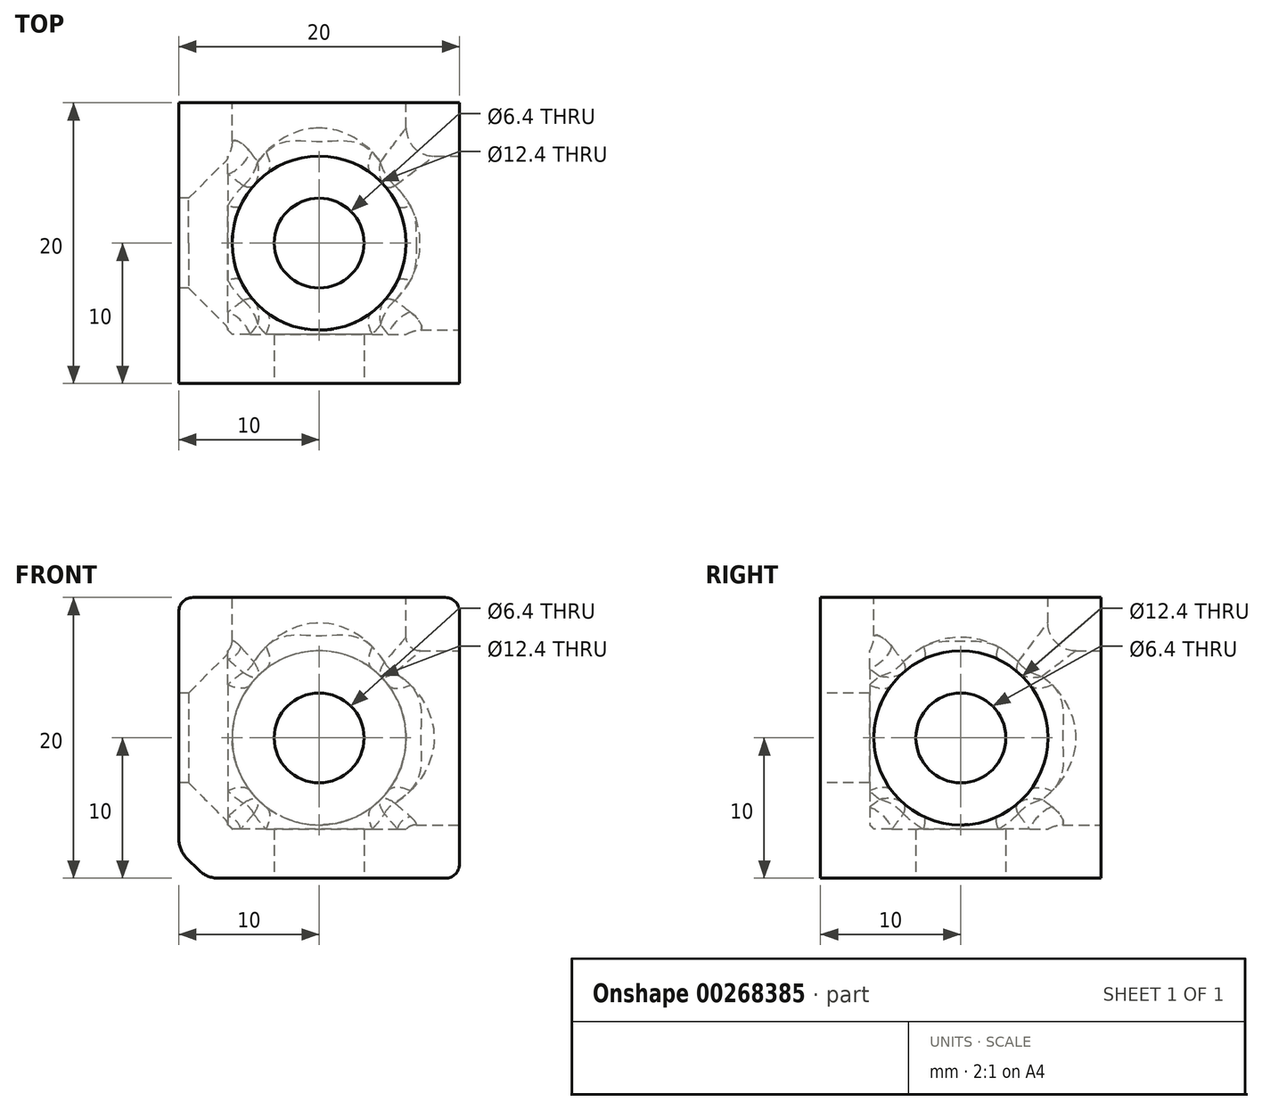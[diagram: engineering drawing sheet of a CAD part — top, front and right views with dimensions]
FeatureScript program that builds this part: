
annotation { "Feature Type Name" : "Feature", "Feature Type Description" : "" }
export const myFeature = defineFeature(function(context is Context, id is Id, definition is map)
    precondition{}
    {
        {
            var Q0;
            Q0=qCreatedBy(makeId("Top.planeOp"),FACE);
            var sketch = newSketch(context, id + "F0", { "sketchPlane" : qUnion([Q0])});
            skLineSegment(sketch, "E0.bottom", {"start": v(10, -10) * mm, "end": v(-10, -10) * mm});
            skLineSegment(sketch, "E0.top", {"start": v(10, 10) * mm, "end": v(-10, 10) * mm});
            skLineSegment(sketch, "E0.left", {"start": v(10, -10) * mm, "end": v(10, 10) * mm});
            skLineSegment(sketch, "E0.right", {"start": v(-10, -10) * mm, "end": v(-10, 10) * mm});
            skPoint(sketch, "E0.middle", {"position": v(0, 0) * mm});
            skSolve(sketch);
        }
        {
            var Q0;
            Q0=qSketchRegion(id+"F0",true);
            extrude(context, id + "F1", {"entities" : qUnion([Q0]), "depth" : 20 * mm});
        }
        {
            var Q0;
            Q0=makeQuery(id+"F1.opExtrude","SWEPT_FACE",FACE,{"disambiguationData":[OSD([sQuery(id+"F0.wireOp",EDGE,"E0.bottom")])]});
            var sketch = newSketch(context, id + "F2", { "sketchPlane" : qUnion([Q0])});
            skCircle(sketch, "E1", {"center": v(0, 10) * mm, "radius": 3.2 * mm});
            skPoint(sketch, "E1.centerSnap0", {"position": v(-10, 10) * mm});
            skSolve(sketch);
        }
        {
            var Q0;
            Q0=makeQuery(id+"F1.opExtrude","SWEPT_FACE",FACE,{"disambiguationData":[OSD([sQuery(id+"F0.wireOp",EDGE,"E0.right")])]});
            var sketch = newSketch(context, id + "F3", { "sketchPlane" : qUnion([Q0])});
            skCircle(sketch, "E2", {"center": v(0, 10) * mm, "radius": 3.2 * mm});
            skPoint(sketch, "E2.centerSnap0", {"position": v(0, 20) * mm});
            skPoint(sketch, "E2.centerSnap1", {"position": v(10, 10) * mm});
            skSolve(sketch);
        }
        {
            var Q0;
            Q0=makeQuery(id+"F1.opExtrude","CAP_FACE",FACE,{"disambiguationData":[OSD([sQuery(id+"F0.wireOp",EDGE,"E0.bottom"),sQuery(id+"F0.wireOp",EDGE,"E0.top"),sQuery(id+"F0.wireOp",EDGE,"E0.left"),sQuery(id+"F0.wireOp",EDGE,"E0.right")])],"isStart":true});
            var sketch = newSketch(context, id + "F4", { "sketchPlane" : qUnion([Q0])});
            skCircle(sketch, "E3", {"center": v(0, 0) * mm, "radius": 3.2 * mm});
            skSolve(sketch);
        }
        {
            var Q0;
            Q0=qSketchRegion(id+"F4",true);
            extrude(context, id + "F5", {"entities" : qUnion([Q0]), "operationType" : NewBodyOperationType.REMOVE, "endBound" : BoundingType.THROUGH_ALL, "oppositeDirection" : true, "depth" : 25 * mm});
        }
        {
            var Q0;
            Q0=makeQuery(id+"F2.imprint","IMPRINT",FACE,{"disambiguationData":[TD([[makeQuery(id+"F2.imprint","IMPRINT",EDGE,{"derivedFrom":sQuery(id+"F2.wireOp",EDGE,"E1")}),1.0]])]});
            extrude(context, id + "F6", {"entities" : qUnion([Q0]), "operationType" : NewBodyOperationType.REMOVE, "endBound" : BoundingType.THROUGH_ALL, "oppositeDirection" : true, "depth" : 25 * mm});
        }
        {
            var Q0;
            Q0=makeQuery(id+"F3.imprint","IMPRINT",FACE,{"disambiguationData":[TD([[makeQuery(id+"F3.imprint","IMPRINT",EDGE,{"derivedFrom":sQuery(id+"F3.wireOp",EDGE,"E2")}),1.0]])]});
            extrude(context, id + "F7", {"entities" : qUnion([Q0]), "operationType" : NewBodyOperationType.REMOVE, "endBound" : BoundingType.THROUGH_ALL, "oppositeDirection" : true, "depth" : 25 * mm});
        }
        {
            var Q0;
            Q0=makeQuery(id+"F1.opExtrude","CAP_FACE",FACE,{"disambiguationData":[OSD([sQuery(id+"F0.wireOp",EDGE,"E0.bottom"),sQuery(id+"F0.wireOp",EDGE,"E0.top"),sQuery(id+"F0.wireOp",EDGE,"E0.left"),sQuery(id+"F0.wireOp",EDGE,"E0.right")])],"isStart":false});
            var sketch = newSketch(context, id + "F8", { "sketchPlane" : qUnion([Q0])});
            skCircle(sketch, "E4", {"center": v(0, 0) * mm, "radius": 6.2 * mm});
            skSolve(sketch);
        }
        {
            var Q0;
            Q0=makeQuery(id+"F1.opExtrude","SWEPT_FACE",FACE,{"disambiguationData":[OSD([sQuery(id+"F0.wireOp",EDGE,"E0.top")])]});
            var sketch = newSketch(context, id + "F9", { "sketchPlane" : qUnion([Q0])});
            skCircle(sketch, "E5", {"center": v(0, 10) * mm, "radius": 6.2 * mm});
            skSolve(sketch);
        }
        {
            var Q0;
            Q0=makeQuery(id+"F1.opExtrude","SWEPT_FACE",FACE,{"disambiguationData":[OSD([sQuery(id+"F0.wireOp",EDGE,"E0.left")])]});
            var sketch = newSketch(context, id + "F10", { "sketchPlane" : qUnion([Q0])});
            skCircle(sketch, "E6", {"center": v(0, 10) * mm, "radius": 6.2 * mm});
            skSolve(sketch);
        }
        {
            var Q0;
            Q0=qSketchRegion(id+"F10",true);
            extrude(context, id + "F11", {"entities" : qUnion([Q0]), "operationType" : NewBodyOperationType.REMOVE, "oppositeDirection" : true, "depth" : 16.5 * mm});
        }
        {
            var Q0;
            Q0=makeQuery(id+"F9.imprint","IMPRINT",FACE,{"disambiguationData":[TD([[makeQuery(id+"F9.imprint","IMPRINT",EDGE,{"derivedFrom":sQuery(id+"F9.wireOp",EDGE,"E5")}),1.0]])]});
            extrude(context, id + "F12", {"entities" : qUnion([Q0]), "operationType" : NewBodyOperationType.REMOVE, "oppositeDirection" : true, "depth" : 16.5 * mm});
        }
        {
            var Q0;
            Q0=makeQuery(id+"F8.imprint","IMPRINT",FACE,{"disambiguationData":[TD([[makeQuery(id+"F8.imprint","IMPRINT",EDGE,{"derivedFrom":sQuery(id+"F8.wireOp",EDGE,"E4")}),1.0]])]});
            extrude(context, id + "F13", {"entities" : qUnion([Q0]), "operationType" : NewBodyOperationType.REMOVE, "oppositeDirection" : true, "depth" : 16.5 * mm});
        }
        {
            var Q0;
            Q0=makeQuery(id+"F11.boolean.opBoolean","INTERSECT",EDGE,{"derivedFrom":[makeQuery(id+"F7.boolean.opBoolean","COPY",FACE,{"disambiguationData":[TD([makeQuery(id+"F1.opExtrude","SWEPT_FACE",FACE,{"disambiguationData":[OSD([sQuery(id+"F0.wireOp",EDGE,"E0.right")])]})])],"derivedFrom":makeQuery(id+"F7.opExtrude","SWEPT_FACE",FACE,{"disambiguationData":[OSD([sQuery(id+"F3.wireOp",EDGE,"E2")])]})}),makeQuery(id+"F11.opExtrude","CAP_FACE",FACE,{"disambiguationData":[OSD([sQuery(id+"F10.wireOp",EDGE,"E6")])],"isStart":false})]});
            var Q1;
            Q1=makeQuery(id+"F13.boolean.opBoolean","COPY",EDGE,{"derivedFrom":makeQuery(id+"F13.opExtrude","CAP_EDGE",EDGE,{"disambiguationData":[OSD([sQuery(id+"F0.wireOp",EDGE,"E0.bottom"),sQuery(id+"F0.wireOp",EDGE,"E0.top"),sQuery(id+"F0.wireOp",EDGE,"E0.left"),sQuery(id+"F0.wireOp",EDGE,"E0.right"),sQuery(id+"F4.wireOp",EDGE,"E3")])],"isStart":false})});
            var Q2;
            Q2=makeQuery(id+"F12.boolean.opBoolean","COPY",EDGE,{"derivedFrom":makeQuery(id+"F12.opExtrude","CAP_EDGE",EDGE,{"disambiguationData":[OSD([sQuery(id+"F0.wireOp",EDGE,"E0.top"),sQuery(id+"F2.wireOp",EDGE,"E1")])],"isStart":false})});
            chamfer(context, id + "F14", {"entities" : qUnion([Q0, Q1, Q2]), "width" : 2.8 * mm, "tangentPropagation" : true});
        }
        {
            var Q0;
            Q0=makeQuery(id+"F1.opExtrude","CAP_EDGE",EDGE,{"disambiguationData":[OSD([sQuery(id+"F0.wireOp",EDGE,"E0.right")])],"isStart":true});
            chamfer(context, id + "F15", {"entities" : qUnion([Q0]), "width" : 2 * mm, "tangentPropagation" : true});
        }
        {
            var Q0;
            {var subQ0=sQuery(id+"F0.wireOp",EDGE,"E0.right");Q0=makeQuery(id+"F15.opChamfer","BLEND_EDGE",EDGE,{"blendedFrom":[makeQuery(id+"F1.opExtrude","CAP_EDGE",EDGE,{"disambiguationData":[OSD([subQ0])],"isStart":true}),makeQuery(id+"F1.opExtrude","CAP_FACE",FACE,{"disambiguationData":[OSD([sQuery(id+"F0.wireOp",EDGE,"E0.bottom"),sQuery(id+"F0.wireOp",EDGE,"E0.top"),sQuery(id+"F0.wireOp",EDGE,"E0.left"),subQ0])],"isStart":true})],"blendedInto":[makeQuery(id+"F1.opExtrude","CAP_FACE",FACE,{"disambiguationData":[OSD([sQuery(id+"F0.wireOp",EDGE,"E0.bottom"),sQuery(id+"F0.wireOp",EDGE,"E0.top"),sQuery(id+"F0.wireOp",EDGE,"E0.left"),subQ0])],"isStart":true})]});}
            var Q1;
            {var subQ0=sQuery(id+"F0.wireOp",EDGE,"E0.right");Q1=makeQuery(id+"F15.opChamfer","BLEND_EDGE",EDGE,{"blendedFrom":[makeQuery(id+"F1.opExtrude","CAP_EDGE",EDGE,{"disambiguationData":[OSD([subQ0])],"isStart":true}),makeQuery(id+"F1.opExtrude","SWEPT_FACE",FACE,{"disambiguationData":[OSD([subQ0])]})],"blendedInto":[makeQuery(id+"F1.opExtrude","SWEPT_FACE",FACE,{"disambiguationData":[OSD([subQ0])]})]});}
            fillet(context, id + "F16", {"entities" : qUnion([Q0, Q1]), "radius" : 2 * mm, "tangentPropagation" : true, "allowEdgeOverflow" : false});
        }
        {
            var Q0;
            {var subQ0=sQuery(id+"F9.wireOp",EDGE,"E5");Q0=makeQuery(id+"F13.boolean.opBoolean","INTERSECT",EDGE,{"disambiguationData":[OD(1.0)],"derivedFrom":[makeQuery(id+"F12.boolean.opBoolean","COPY",FACE,{"disambiguationData":[TD([makeQuery(id+"F12.opExtrude","CAP_FACE",FACE,{"disambiguationData":[OSD([sQuery(id+"F0.wireOp",EDGE,"E0.top"),sQuery(id+"F2.wireOp",EDGE,"E1"),subQ0])],"isStart":false})])],"derivedFrom":makeQuery(id+"F12.opExtrude","SWEPT_FACE",FACE,{"disambiguationData":[OSD([subQ0])]})}),makeQuery(id+"F13.opExtrude","SWEPT_FACE",FACE,{"disambiguationData":[OSD([sQuery(id+"F8.wireOp",EDGE,"E4")])]})]});}
            var Q1;
            Q1=makeQuery(id+"F12.boolean.opBoolean","INTERSECT",EDGE,{"disambiguationData":[OD(3.0)],"derivedFrom":[makeQuery(id+"F11.boolean.opBoolean","COPY",FACE,{"derivedFrom":makeQuery(id+"F11.opExtrude","SWEPT_FACE",FACE,{"disambiguationData":[OSD([sQuery(id+"F10.wireOp",EDGE,"E6")])]})}),makeQuery(id+"F12.opExtrude","SWEPT_FACE",FACE,{"disambiguationData":[OSD([sQuery(id+"F9.wireOp",EDGE,"E5")])]})]});
            var Q2;
            Q2=makeQuery(id+"F12.boolean.opBoolean","INTERSECT",EDGE,{"disambiguationData":[OD(1.0)],"derivedFrom":[makeQuery(id+"F11.boolean.opBoolean","COPY",FACE,{"derivedFrom":makeQuery(id+"F11.opExtrude","SWEPT_FACE",FACE,{"disambiguationData":[OSD([sQuery(id+"F10.wireOp",EDGE,"E6")])]})}),makeQuery(id+"F12.opExtrude","SWEPT_FACE",FACE,{"disambiguationData":[OSD([sQuery(id+"F9.wireOp",EDGE,"E5")])]})]});
            var Q3;
            {var subQ0=sQuery(id+"F9.wireOp",EDGE,"E5");Q3=makeQuery(id+"F13.boolean.opBoolean","INTERSECT",EDGE,{"disambiguationData":[OD(0.0)],"derivedFrom":[makeQuery(id+"F12.boolean.opBoolean","COPY",FACE,{"disambiguationData":[TD([makeQuery(id+"F12.opExtrude","CAP_FACE",FACE,{"disambiguationData":[OSD([sQuery(id+"F0.wireOp",EDGE,"E0.top"),sQuery(id+"F2.wireOp",EDGE,"E1"),subQ0])],"isStart":false})])],"derivedFrom":makeQuery(id+"F12.opExtrude","SWEPT_FACE",FACE,{"disambiguationData":[OSD([subQ0])]})}),makeQuery(id+"F13.opExtrude","SWEPT_FACE",FACE,{"disambiguationData":[OSD([sQuery(id+"F8.wireOp",EDGE,"E4")])]})]});}
            fillet(context, id + "F17", {"entities" : qUnion([Q0, Q1, Q2, Q3]), "radius" : 2 * mm, "tangentPropagation" : true, "allowEdgeOverflow" : false});
        }
        {
            var Q0;
            Q0=makeQuery(id+"F13.boolean.opBoolean","INTERSECT",EDGE,{"disambiguationData":[OD(1.0)],"derivedFrom":[makeQuery(id+"F12.boolean.opBoolean","COPY",FACE,{"disambiguationData":[TD([makeQuery(id+"F1.opExtrude","SWEPT_FACE",FACE,{"disambiguationData":[OSD([sQuery(id+"F0.wireOp",EDGE,"E0.top")])]})])],"derivedFrom":makeQuery(id+"F12.opExtrude","SWEPT_FACE",FACE,{"disambiguationData":[OSD([sQuery(id+"F9.wireOp",EDGE,"E5")])]})}),makeQuery(id+"F13.opExtrude","SWEPT_FACE",FACE,{"disambiguationData":[OSD([sQuery(id+"F8.wireOp",EDGE,"E4")])]})]});
            var Q1;
            Q1=makeQuery(id+"F12.boolean.opBoolean","INTERSECT",EDGE,{"disambiguationData":[OD(2.0)],"derivedFrom":[makeQuery(id+"F11.boolean.opBoolean","COPY",FACE,{"derivedFrom":makeQuery(id+"F11.opExtrude","SWEPT_FACE",FACE,{"disambiguationData":[OSD([sQuery(id+"F10.wireOp",EDGE,"E6")])]})}),makeQuery(id+"F12.opExtrude","SWEPT_FACE",FACE,{"disambiguationData":[OSD([sQuery(id+"F9.wireOp",EDGE,"E5")])]})]});
            var Q2;
            Q2=makeQuery(id+"F12.boolean.opBoolean","INTERSECT",EDGE,{"disambiguationData":[OD(0.0)],"derivedFrom":[makeQuery(id+"F11.boolean.opBoolean","COPY",FACE,{"derivedFrom":makeQuery(id+"F11.opExtrude","SWEPT_FACE",FACE,{"disambiguationData":[OSD([sQuery(id+"F10.wireOp",EDGE,"E6")])]})}),makeQuery(id+"F12.opExtrude","SWEPT_FACE",FACE,{"disambiguationData":[OSD([sQuery(id+"F9.wireOp",EDGE,"E5")])]})]});
            var Q3;
            Q3=makeQuery(id+"F13.boolean.opBoolean","INTERSECT",EDGE,{"disambiguationData":[OD(0.0)],"derivedFrom":[makeQuery(id+"F12.boolean.opBoolean","COPY",FACE,{"disambiguationData":[TD([makeQuery(id+"F1.opExtrude","SWEPT_FACE",FACE,{"disambiguationData":[OSD([sQuery(id+"F0.wireOp",EDGE,"E0.top")])]})])],"derivedFrom":makeQuery(id+"F12.opExtrude","SWEPT_FACE",FACE,{"disambiguationData":[OSD([sQuery(id+"F9.wireOp",EDGE,"E5")])]})}),makeQuery(id+"F13.opExtrude","SWEPT_FACE",FACE,{"disambiguationData":[OSD([sQuery(id+"F8.wireOp",EDGE,"E4")])]})]});
            fillet(context, id + "F18", {"entities" : qUnion([Q0, Q1, Q2, Q3]), "radius" : 2 * mm, "tangentPropagation" : true, "allowEdgeOverflow" : false});
        }
        {
            var Q0;
            {var subQ0=sQuery(id+"F10.wireOp",EDGE,"E6");Q0=makeQuery(id+"F13.boolean.opBoolean","INTERSECT",EDGE,{"disambiguationData":[OD(0.0)],"derivedFrom":[makeQuery(id+"F12.boolean.opBoolean","SPLIT",FACE,{"disambiguationData":[TD([makeQuery(id+"F11.boolean.opBoolean","COPY",FACE,{"derivedFrom":makeQuery(id+"F11.opExtrude","CAP_FACE",FACE,{"disambiguationData":[OSD([subQ0])],"isStart":false})})])],"derivedFrom":makeQuery(id+"F11.boolean.opBoolean","COPY",FACE,{"derivedFrom":makeQuery(id+"F11.opExtrude","SWEPT_FACE",FACE,{"disambiguationData":[OSD([subQ0])]})})}),makeQuery(id+"F13.opExtrude","SWEPT_FACE",FACE,{"disambiguationData":[OSD([sQuery(id+"F8.wireOp",EDGE,"E4")])]})]});}
            var Q1;
            {var subQ0=sQuery(id+"F10.wireOp",EDGE,"E6");Q1=makeQuery(id+"F13.boolean.opBoolean","INTERSECT",EDGE,{"disambiguationData":[OD(1.0)],"derivedFrom":[makeQuery(id+"F12.boolean.opBoolean","SPLIT",FACE,{"disambiguationData":[TD([makeQuery(id+"F11.boolean.opBoolean","COPY",FACE,{"derivedFrom":makeQuery(id+"F11.opExtrude","CAP_FACE",FACE,{"disambiguationData":[OSD([subQ0])],"isStart":false})})])],"derivedFrom":makeQuery(id+"F11.boolean.opBoolean","COPY",FACE,{"derivedFrom":makeQuery(id+"F11.opExtrude","SWEPT_FACE",FACE,{"disambiguationData":[OSD([subQ0])]})})}),makeQuery(id+"F13.opExtrude","SWEPT_FACE",FACE,{"disambiguationData":[OSD([sQuery(id+"F8.wireOp",EDGE,"E4")])]})]});}
            var Q2;
            Q2=makeQuery(id+"F13.boolean.opBoolean","INTERSECT",EDGE,{"disambiguationData":[OD(0.0)],"derivedFrom":[makeQuery(id+"F12.boolean.opBoolean","SPLIT",FACE,{"disambiguationData":[TD([makeQuery(id+"F1.opExtrude","SWEPT_FACE",FACE,{"disambiguationData":[OSD([sQuery(id+"F0.wireOp",EDGE,"E0.left")])]})])],"derivedFrom":makeQuery(id+"F11.boolean.opBoolean","COPY",FACE,{"derivedFrom":makeQuery(id+"F11.opExtrude","SWEPT_FACE",FACE,{"disambiguationData":[OSD([sQuery(id+"F10.wireOp",EDGE,"E6")])]})})}),makeQuery(id+"F13.opExtrude","SWEPT_FACE",FACE,{"disambiguationData":[OSD([sQuery(id+"F8.wireOp",EDGE,"E4")])]})]});
            var Q3;
            Q3=makeQuery(id+"F13.boolean.opBoolean","INTERSECT",EDGE,{"disambiguationData":[OD(1.0)],"derivedFrom":[makeQuery(id+"F12.boolean.opBoolean","SPLIT",FACE,{"disambiguationData":[TD([makeQuery(id+"F1.opExtrude","SWEPT_FACE",FACE,{"disambiguationData":[OSD([sQuery(id+"F0.wireOp",EDGE,"E0.left")])]})])],"derivedFrom":makeQuery(id+"F11.boolean.opBoolean","COPY",FACE,{"derivedFrom":makeQuery(id+"F11.opExtrude","SWEPT_FACE",FACE,{"disambiguationData":[OSD([sQuery(id+"F10.wireOp",EDGE,"E6")])]})})}),makeQuery(id+"F13.opExtrude","SWEPT_FACE",FACE,{"disambiguationData":[OSD([sQuery(id+"F8.wireOp",EDGE,"E4")])]})]});
            fillet(context, id + "F19", {"entities" : qUnion([Q0, Q1, Q2, Q3]), "radius" : 1 * mm, "tangentPropagation" : true, "allowEdgeOverflow" : false});
        }
        {
            var Q0;
            {var subQ0=makeQuery(id+"F11.opExtrude","CAP_FACE",FACE,{"disambiguationData":[OSD([sQuery(id+"F10.wireOp",EDGE,"E6")])],"isStart":false});Q0=makeQuery(id+"F14.opChamfer","BLEND_EDGE",EDGE,{"blendedFrom":[makeQuery(id+"F11.boolean.opBoolean","INTERSECT",EDGE,{"derivedFrom":[makeQuery(id+"F7.boolean.opBoolean","COPY",FACE,{"disambiguationData":[TD([makeQuery(id+"F1.opExtrude","SWEPT_FACE",FACE,{"disambiguationData":[OSD([sQuery(id+"F0.wireOp",EDGE,"E0.right")])]})])],"derivedFrom":makeQuery(id+"F7.opExtrude","SWEPT_FACE",FACE,{"disambiguationData":[OSD([sQuery(id+"F3.wireOp",EDGE,"E2")])]})}),subQ0]}),makeQuery(id+"F11.boolean.opBoolean","COPY",FACE,{"derivedFrom":subQ0})],"blendedInto":[makeQuery(id+"F11.boolean.opBoolean","COPY",FACE,{"derivedFrom":subQ0})]});}
            var Q1;
            {var subQ0=sQuery(id+"F2.wireOp",EDGE,"E1");var subQ1=sQuery(id+"F0.wireOp",EDGE,"E0.top");Q1=makeQuery(id+"F14.opChamfer","BLEND_EDGE",EDGE,{"blendedFrom":[makeQuery(id+"F12.boolean.opBoolean","COPY",EDGE,{"derivedFrom":makeQuery(id+"F12.opExtrude","CAP_EDGE",EDGE,{"disambiguationData":[OSD([subQ1,subQ0])],"isStart":false})}),makeQuery(id+"F12.boolean.opBoolean","COPY",FACE,{"derivedFrom":makeQuery(id+"F12.opExtrude","CAP_FACE",FACE,{"disambiguationData":[OSD([subQ1,subQ0,sQuery(id+"F9.wireOp",EDGE,"E5")])],"isStart":false})})],"blendedInto":[makeQuery(id+"F12.boolean.opBoolean","COPY",FACE,{"derivedFrom":makeQuery(id+"F12.opExtrude","CAP_FACE",FACE,{"disambiguationData":[OSD([subQ1,subQ0,sQuery(id+"F9.wireOp",EDGE,"E5")])],"isStart":false})})]});}
            var Q2;
            {var subQ0=sQuery(id+"F4.wireOp",EDGE,"E3");var subQ1=sQuery(id+"F0.wireOp",EDGE,"E0.right");var subQ2=sQuery(id+"F0.wireOp",EDGE,"E0.left");var subQ3=sQuery(id+"F0.wireOp",EDGE,"E0.top");var subQ4=sQuery(id+"F0.wireOp",EDGE,"E0.bottom");Q2=makeQuery(id+"F14.opChamfer","BLEND_EDGE",EDGE,{"blendedFrom":[makeQuery(id+"F13.boolean.opBoolean","COPY",EDGE,{"derivedFrom":makeQuery(id+"F13.opExtrude","CAP_EDGE",EDGE,{"disambiguationData":[OSD([subQ4,subQ3,subQ2,subQ1,subQ0])],"isStart":false})}),makeQuery(id+"F13.boolean.opBoolean","COPY",FACE,{"derivedFrom":makeQuery(id+"F13.opExtrude","CAP_FACE",FACE,{"disambiguationData":[OSD([subQ4,subQ3,subQ2,subQ1,subQ0,sQuery(id+"F8.wireOp",EDGE,"E4")])],"isStart":false})})],"blendedInto":[makeQuery(id+"F13.boolean.opBoolean","COPY",FACE,{"derivedFrom":makeQuery(id+"F13.opExtrude","CAP_FACE",FACE,{"disambiguationData":[OSD([subQ4,subQ3,subQ2,subQ1,subQ0,sQuery(id+"F8.wireOp",EDGE,"E4")])],"isStart":false})})]});}
            fillet(context, id + "F20", {"entities" : qUnion([Q0, Q1, Q2]), "radius" : 0.5 * mm, "tangentPropagation" : true, "allowEdgeOverflow" : false});
        }
        {
            var Q0;
            Q0=makeQuery(id+"F1.opExtrude","CAP_EDGE",EDGE,{"disambiguationData":[OSD([sQuery(id+"F0.wireOp",EDGE,"E0.left")])],"isStart":true});
            var Q1;
            Q1=makeQuery(id+"F1.opExtrude","CAP_EDGE",EDGE,{"disambiguationData":[OSD([sQuery(id+"F0.wireOp",EDGE,"E0.left")])],"isStart":false});
            var Q2;
            Q2=makeQuery(id+"F1.opExtrude","CAP_EDGE",EDGE,{"disambiguationData":[OSD([sQuery(id+"F0.wireOp",EDGE,"E0.right")])],"isStart":false});
            fillet(context, id + "F21", {"entities" : qUnion([Q0, Q1, Q2]), "radius" : 1 * mm, "tangentPropagation" : true, "allowEdgeOverflow" : false});
        }
    });
